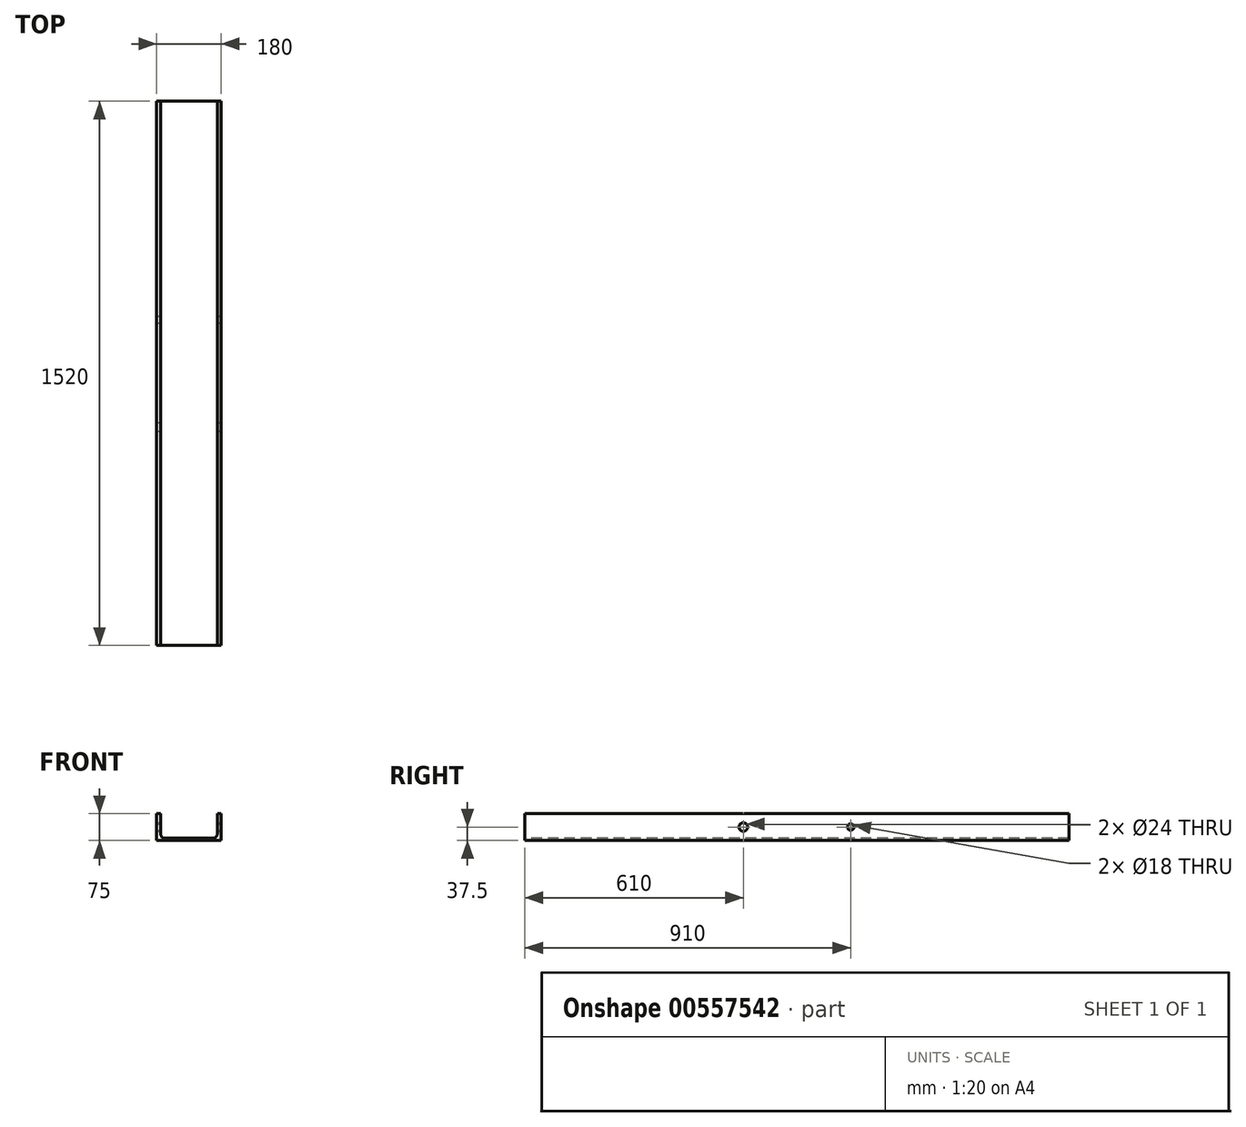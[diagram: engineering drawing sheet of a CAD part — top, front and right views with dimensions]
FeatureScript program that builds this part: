
annotation { "Feature Type Name" : "Feature", "Feature Type Description" : "" }
export const myFeature = defineFeature(function(context is Context, id is Id, definition is map)
    precondition{}
    {
        {
            var Q0;
            Q0=qCreatedBy(makeId("Front.planeOp"),FACE);
            var sketch = newSketch(context, id + "F0", { "sketchPlane" : qUnion([Q0])});
            skLineSegment(sketch, "E0", {"start": v(0, 0) * mm, "end": v(-180, 0) * mm});
            skLineSegment(sketch, "E1", {"start": v(-180, 0) * mm, "end": v(-180, 75) * mm});
            skLineSegment(sketch, "E2", {"start": v(-180, 75) * mm, "end": v(-169, 75) * mm});
            skLineSegment(sketch, "E3", {"start": v(-169, 75) * mm, "end": v(-169, 18) * mm});
            skLineSegment(sketch, "E4", {"start": v(-157, 6) * mm, "end": v(-23, 6) * mm});
            skLineSegment(sketch, "E5", {"start": v(-11, 18) * mm, "end": v(-11, 75) * mm});
            skLineSegment(sketch, "E6", {"start": v(-11, 75) * mm, "end": v(0, 75) * mm});
            skLineSegment(sketch, "E7", {"start": v(0, 75) * mm, "end": v(0, 0) * mm});
            skPoint(sketch, "E8.visualSharp", {"position": v(-169, 6) * mm});
            skArc(sketch, "E8.filletArc", {"start": v(-169, 18) * mm, "mid": v(-165.49, 9.51) * mm, "end": v(-157, 6) * mm});
            skPoint(sketch, "E9.visualSharp", {"position": v(-11, 6) * mm});
            skArc(sketch, "E9.filletArc", {"start": v(-23, 6) * mm, "mid": v(-14.51, 9.51) * mm, "end": v(-11, 18) * mm});
            skSolve(sketch);
        }
        {
            var Q0;
            Q0=makeQuery(id+"F0.imprint","IMPRINT",FACE,{"disambiguationData":[TD([[makeQuery(id+"F0.imprint","IMPRINT",EDGE,{"derivedFrom":sQuery(id+"F0.wireOp",EDGE,"E0")}),-1.0]])]});
            extrude(context, id + "F1", {"entities" : qUnion([Q0]), "oppositeDirection" : true, "depth" : 1520 * mm, "offsetDistance" : 25 * mm});
        }
        {
            var Q0;
            Q0=makeQuery(id+"F1.opExtrude","SWEPT_FACE",FACE,{"disambiguationData":[OSD([sQuery(id+"F0.wireOp",EDGE,"E7")])]});
            var sketch = newSketch(context, id + "F2", { "sketchPlane" : qUnion([Q0])});
            skCircle(sketch, "E10", {"center": v(910, 37.5) * mm, "radius": 9 * mm});
            skCircle(sketch, "E11", {"center": v(610, 37.5) * mm, "radius": 12 * mm});
            skSolve(sketch);
        }
        {
            var Q0;
            Q0 = qSketchRegion(id + "F2", true);
            extrude(context, id + "F3", {"entities" : qUnion([Q0]), "operationType" : NewBodyOperationType.REMOVE, "oppositeDirection" : true, "depth" : 180 * mm, "offsetDistance" : 25 * mm});
        }
    });
